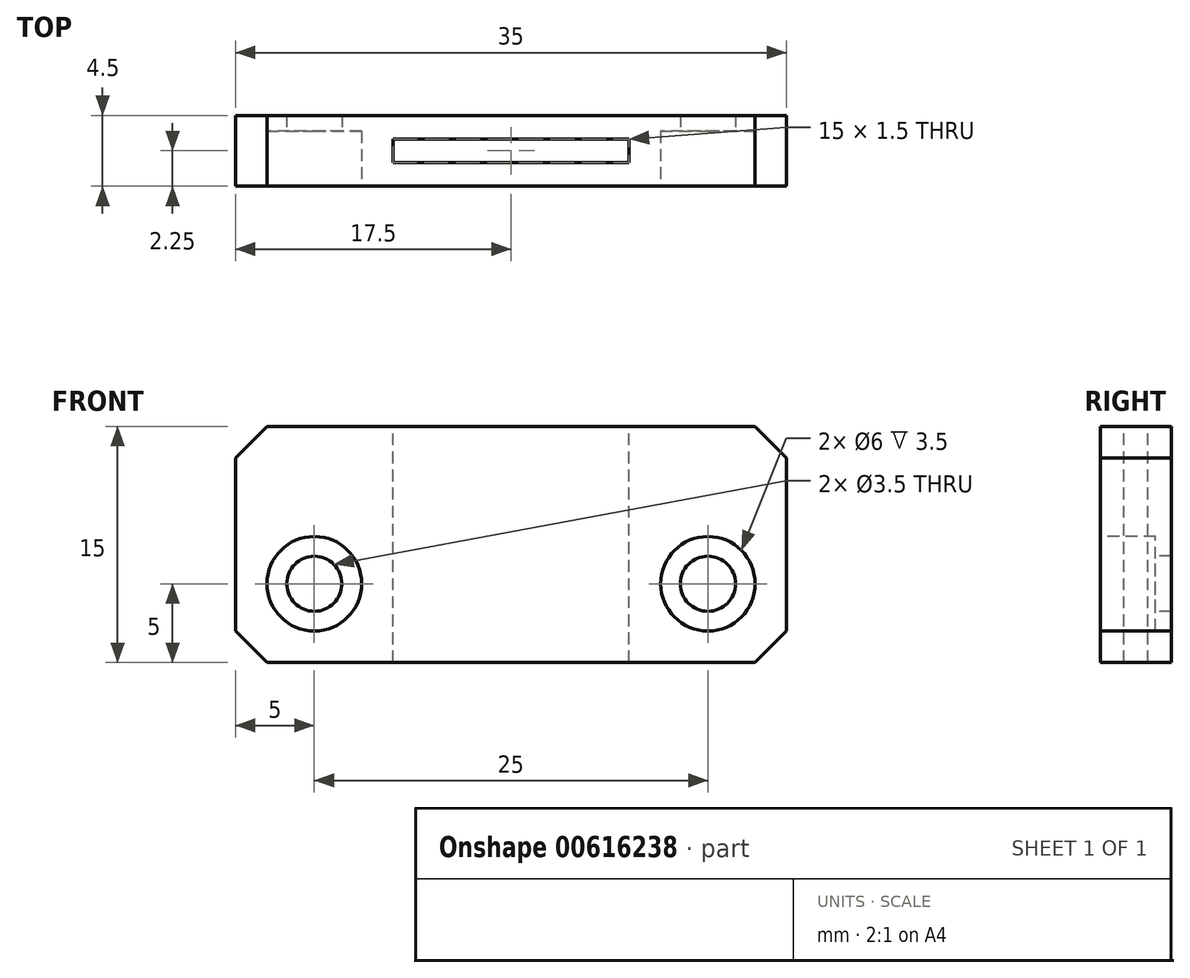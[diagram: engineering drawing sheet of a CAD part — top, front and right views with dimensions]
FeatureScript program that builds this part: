
annotation { "Feature Type Name" : "Feature", "Feature Type Description" : "" }
export const myFeature = defineFeature(function(context is Context, id is Id, definition is map)
    precondition{}
    {
        {
            var Q0;
            Q0=qCreatedBy(makeId("Front.planeOp"),FACE);
            var sketch = newSketch(context, id + "F0", { "sketchPlane" : qUnion([Q0])});
            skLineSegment(sketch, "E0.bottom", {"start": v(-17.5, 7.5) * mm, "end": v(17.5, 7.5) * mm});
            skLineSegment(sketch, "E0.top", {"start": v(-17.5, -7.5) * mm, "end": v(17.5, -7.5) * mm});
            skLineSegment(sketch, "E0.left", {"start": v(-17.5, 7.5) * mm, "end": v(-17.5, -7.5) * mm});
            skLineSegment(sketch, "E0.right", {"start": v(17.5, 7.5) * mm, "end": v(17.5, -7.5) * mm});
            skPoint(sketch, "E0.middle", {"position": v(0, 0) * mm});
            skSolve(sketch);
        }
        {
            var Q0;
            Q0=makeQuery(id+"F0.imprint","IMPRINT",FACE,{"disambiguationData":[TD([[makeQuery(id+"F0.imprint","IMPRINT",EDGE,{"derivedFrom":sQuery(id+"F0.wireOp",EDGE,"E0.bottom")}),-1.0]])]});
            extrude(context, id + "F1", {"entities" : qUnion([Q0]), "depth" : 4.5 * mm, "offsetDistance" : 25 * mm});
        }
        {
            var Q0;
            Q0=makeQuery(id+"F1.opExtrude","SWEPT_FACE",FACE,{"disambiguationData":[OSD([sQuery(id+"F0.wireOp",EDGE,"E0.bottom")])]});
            var sketch = newSketch(context, id + "F2", { "sketchPlane" : qUnion([Q0])});
            skLineSegment(sketch, "E1.bottom", {"start": v(-7.5, -1.5) * mm, "end": v(7.5, -1.5) * mm});
            skLineSegment(sketch, "E1.top", {"start": v(-7.5, -3) * mm, "end": v(7.5, -3) * mm});
            skLineSegment(sketch, "E1.left", {"start": v(-7.5, -1.5) * mm, "end": v(-7.5, -3) * mm});
            skLineSegment(sketch, "E1.right", {"start": v(7.5, -1.5) * mm, "end": v(7.5, -3) * mm});
            skPoint(sketch, "E1.middle", {"position": v(0, -2.25) * mm});
            skPoint(sketch, "E1.middle.positionSnap0", {"position": v(17.5, -2.25) * mm});
            skPoint(sketch, "E1.centerSnap0", {"position": v(17.5, -2.25) * mm});
            skSolve(sketch);
        }
        {
            var Q0;
            Q0=qSketchRegion(id+"F2",true);
            extrude(context, id + "F3", {"entities" : qUnion([Q0]), "operationType" : NewBodyOperationType.REMOVE, "endBound" : BoundingType.THROUGH_ALL, "oppositeDirection" : true, "depth" : 25 * mm, "offsetDistance" : 25 * mm});
        }
        {
            var Q0;
            Q0=makeQuery(id+"F1.opExtrude","CAP_FACE",FACE,{"disambiguationData":[OSD([sQuery(id+"F0.wireOp",EDGE,"E0.bottom"),sQuery(id+"F0.wireOp",EDGE,"E0.top"),sQuery(id+"F0.wireOp",EDGE,"E0.left"),sQuery(id+"F0.wireOp",EDGE,"E0.right")])],"isStart":false});
            var sketch = newSketch(context, id + "F4", { "sketchPlane" : qUnion([Q0])});
            skCircle(sketch, "E2", {"center": v(12.5, -2.5) * mm, "radius": 3 * mm});
            skCircle(sketch, "E3.MirrorC", {"center": v(-12.5, -2.5) * mm, "radius": 3 * mm});
            skSolve(sketch);
        }
        {
            var Q0;
            Q0=qSketchRegion(id+"F4",true);
            extrude(context, id + "F5", {"entities" : qUnion([Q0]), "operationType" : NewBodyOperationType.REMOVE, "oppositeDirection" : true, "depth" : 3.5 * mm, "offsetDistance" : 25 * mm});
        }
        {
            var Q0;
            Q0=makeQuery(id+"F1.opExtrude","CAP_FACE",FACE,{"disambiguationData":[OSD([sQuery(id+"F0.wireOp",EDGE,"E0.bottom"),sQuery(id+"F0.wireOp",EDGE,"E0.top"),sQuery(id+"F0.wireOp",EDGE,"E0.left"),sQuery(id+"F0.wireOp",EDGE,"E0.right")])],"isStart":false});
            var sketch = newSketch(context, id + "F6", { "sketchPlane" : qUnion([Q0])});
            skPoint(sketch, "E4", {"position": v(12.5, -2.5) * mm});
            skPoint(sketch, "E5", {"position": v(-12.5, -2.5) * mm});
            skCircle(sketch, "E6", {"center": v(12.5, -2.5) * mm, "radius": 1.75 * mm});
            skCircle(sketch, "E7", {"center": v(-12.5, -2.5) * mm, "radius": 1.75 * mm});
            skSolve(sketch);
        }
        {
            var Q0;
            Q0=qSketchRegion(id+"F6",true);
            extrude(context, id + "F7", {"entities" : qUnion([Q0]), "operationType" : NewBodyOperationType.REMOVE, "endBound" : BoundingType.THROUGH_ALL, "oppositeDirection" : true, "depth" : 25 * mm, "offsetDistance" : 25 * mm});
        }
        {
            var Q0;
            Q0=makeQuery(id+"F1.opExtrude","SWEPT_EDGE",EDGE,{"disambiguationData":[OSD([sQuery(id+"F0.wireOp",EDGE,"E0.bottom"),sQuery(id+"F0.wireOp",EDGE,"E0.left")])]});
            var Q1;
            Q1=makeQuery(id+"F1.opExtrude","SWEPT_EDGE",EDGE,{"disambiguationData":[OSD([sQuery(id+"F0.wireOp",EDGE,"E0.bottom"),sQuery(id+"F0.wireOp",EDGE,"E0.right")])]});
            var Q2;
            Q2=makeQuery(id+"F1.opExtrude","SWEPT_EDGE",EDGE,{"disambiguationData":[OSD([sQuery(id+"F0.wireOp",EDGE,"E0.top"),sQuery(id+"F0.wireOp",EDGE,"E0.right")])]});
            var Q3;
            Q3=makeQuery(id+"F1.opExtrude","SWEPT_EDGE",EDGE,{"disambiguationData":[OSD([sQuery(id+"F0.wireOp",EDGE,"E0.top"),sQuery(id+"F0.wireOp",EDGE,"E0.left")])]});
            chamfer(context, id + "F8", {"entities" : qUnion([Q0, Q1, Q2, Q3]), "width" : 2 * mm, "tangentPropagation" : true});
        }
    });
